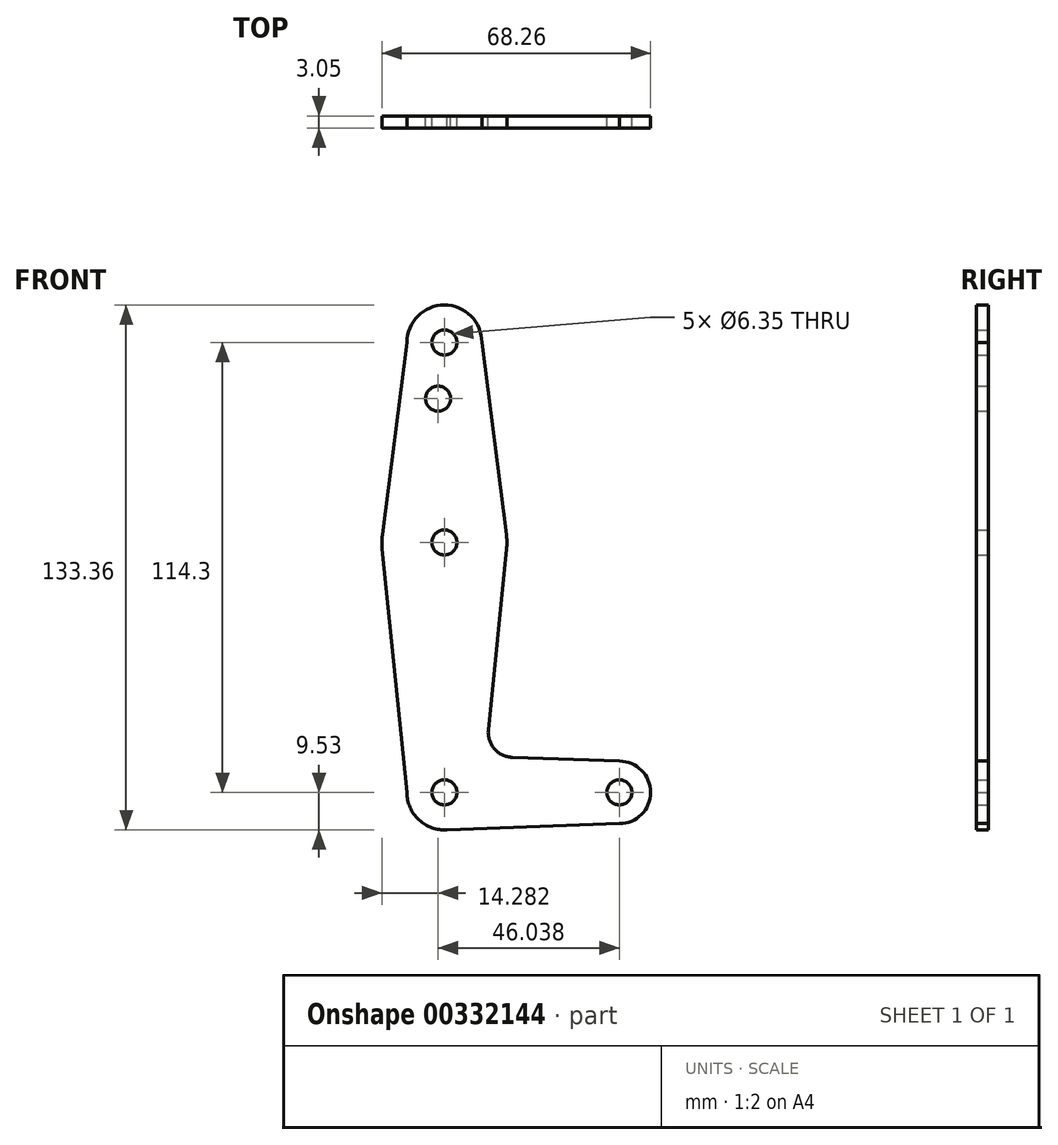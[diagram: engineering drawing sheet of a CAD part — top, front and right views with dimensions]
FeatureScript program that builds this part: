
annotation { "Feature Type Name" : "Feature", "Feature Type Description" : "" }
export const myFeature = defineFeature(function(context is Context, id is Id, definition is map)
    precondition{}
    {
        {
            var Q0;
            Q0=qCreatedBy(makeId("Front.planeOp"),FACE);
            var sketch = newSketch(context, id + "F0", { "sketchPlane" : qUnion([Q0])});
            skLineSegment(sketch, "E0", {"start": v(0, 0) * mm, "end": v(0, 114.3) * mm, "construction": true});
            skLineSegment(sketch, "E1", {"start": v(0, 0) * mm, "end": v(44.45, 0) * mm, "construction": true});
            skCircle(sketch, "E2", {"center": v(0, 114.3) * mm, "radius": 9.53 * mm});
            skCircle(sketch, "E3", {"center": v(0, 0) * mm, "radius": 9.53 * mm});
            skCircle(sketch, "E4", {"center": v(0, 63.5) * mm, "radius": 15.88 * mm});
            skCircle(sketch, "E5", {"center": v(44.45, 0) * mm, "radius": 7.94 * mm});
            skLineSegment(sketch, "E6", {"start": v(-9.53, 114.3) * mm, "end": v(-15.75, 65.5) * mm});
            skLineSegment(sketch, "E7", {"start": v(-9.53, 0) * mm, "end": v(-15.8, 61.9) * mm});
            skLineSegment(sketch, "E8", {"start": v(9.53, 114.3) * mm, "end": v(15.75, 65.5) * mm});
            skLineSegment(sketch, "E9", {"start": v(0, -9.52) * mm, "end": v(44.45, -7.94) * mm});
            skCircle(sketch, "E10", {"center": v(0, 114.3) * mm, "radius": 3.18 * mm});
            skCircle(sketch, "E11", {"center": v(0, 63.5) * mm, "radius": 3.18 * mm});
            skCircle(sketch, "E12", {"center": v(0, 0) * mm, "radius": 3.18 * mm});
            skCircle(sketch, "E13", {"center": v(44.45, 0) * mm, "radius": 3.18 * mm});
            skLineSegment(sketch, "E14", {"start": v(15.8, 61.9) * mm, "end": v(11.17, 15.89) * mm});
            skLineSegment(sketch, "E15", {"start": v(17.26, 8.9) * mm, "end": v(44.45, 7.94) * mm});
            skPoint(sketch, "E16", {"position": v(22.23, 8.73) * mm});
            skCircle(sketch, "E17", {"center": v(-1.59, 100.03) * mm, "radius": 3.18 * mm});
            skPoint(sketch, "E18.newPointB", {"position": v(0, 9.52) * mm});
            skArc(sketch, "E18.filletArc", {"start": v(11.17, 15.89) * mm, "mid": v(12.7, 11.08) * mm, "end": v(17.26, 8.9) * mm});
            skSolve(sketch);
        }
        {
            var Q0;
            Q0 = qSketchRegion(id + "F0", true);
            extrude(context, id + "F1", {"entities" : qUnion([Q0]), "depth" : 3.05 * mm});
        }
    });
